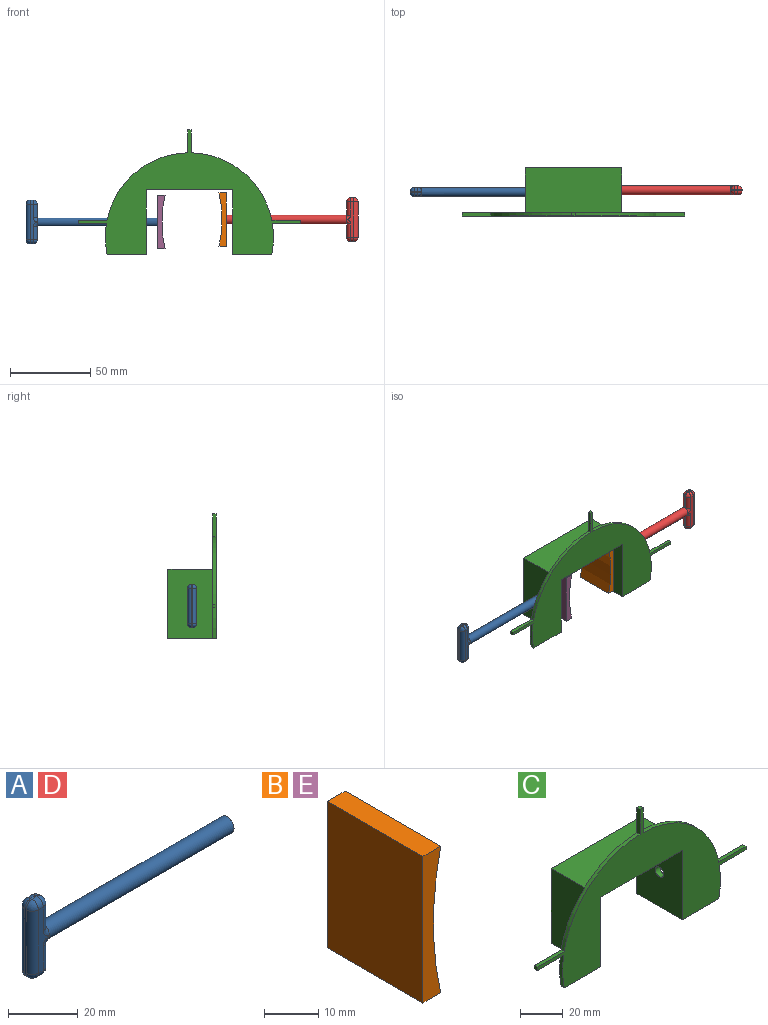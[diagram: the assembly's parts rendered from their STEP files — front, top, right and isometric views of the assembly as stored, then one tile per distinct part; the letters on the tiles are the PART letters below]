
ASSEMBLY  parts=5 mates=4
PART A: 33 faces, bbox 82x5.6x27.3 mm
  f0: plane 8.41x0.6mm, normal (1,0,0), area 5mm2, adj f1,f20,f28,f29
  f1: cylinder r=2.75mm len=75mm, axis (1,0,0), area 1295.9mm2, adj f0,f2,f8,f14,f25
  f2: plane 5.5x5.5mm, normal (1,0,0), area 23.8mm2, adj f1
  f3: plane 22.28x4.01mm, normal (0,1,0), area 47.7mm2, adj f16,f21,f25,f26,f29,f32
  f4: plane 2x0.6mm, normal (0,0,-1), area 1.2mm2, adj f19,f27,f28,f32
  f5: plane 22.28x4.01mm, normal (0,-1,0), area 48.1mm2, adj f10,f11,f14,f18,f19,f20
  f6: plane 2x0.6mm, normal (0,0,1), area 1.2mm2, adj f10,f12,f16,f17
  f7: plane 22.28x0.6mm, normal (-1,0,0), area 13.3mm2, adj f17,f18,f26,f27
  f8: plane 8.41x0.6mm, normal (1,0,0), area 5mm2, adj f1,f11,f12,f21
  f9: sphere r=2.5mm, area 9.8mm2, adj f10,f11,f12
  f10: cylinder r=2.5mm len=2.5mm, axis (1,0,0), area 7.9mm2, adj f5,f6,f9,f13
  f11: cylinder r=2.5mm len=8.41mm, axis (0,0,1), area 33mm2, adj f5,f8,f9,f14
  f12: cylinder r=2.5mm len=2.5mm, axis (0,1,0), area 2.3mm2, adj f6,f8,f9,f15
  f13: sphere r=2.5mm, area 9.8mm2, adj f10,f17,f18
  f14: bspline ~6.17x2.55mm, area 11.9mm2, adj f1,f5,f11,f20
  f15: sphere r=2.5mm, area 9.8mm2, adj f12,f16,f21
  f16: cylinder r=2.5mm len=2.5mm, axis (-1,0,0), area 7.9mm2, adj f3,f6,f15,f22
  f17: cylinder r=2.5mm len=2.5mm, axis (0,-1,0), area 2.3mm2, adj f6,f7,f13,f22
  f18: cylinder r=2.5mm len=22.28mm, axis (0,0,-1), area 87.5mm2, adj f5,f7,f13,f23
  f19: cylinder r=2.5mm len=2.5mm, axis (-1,0,0), area 7.9mm2, adj f4,f5,f23,f24
  f20: cylinder r=2.5mm len=8.41mm, axis (0,0,1), area 33mm2, adj f0,f5,f14,f24
  f21: cylinder r=2.5mm len=8.41mm, axis (0,0,-1), area 33mm2, adj f3,f8,f15,f25
  f22: sphere r=2.5mm, area 9.8mm2, adj f16,f17,f26
  f23: sphere r=2.5mm, area 9.8mm2, adj f18,f19,f27
  f24: sphere r=2.5mm, area 9.8mm2, adj f19,f20,f28
  f25: bspline ~6.17x2.55mm, area 11.9mm2, adj f1,f3,f21,f29
  f26: cylinder r=2.5mm len=22.28mm, axis (0,0,1), area 87.5mm2, adj f3,f7,f22,f30
  f27: cylinder r=2.5mm len=2.5mm, axis (0,1,0), area 2.3mm2, adj f4,f7,f23,f30
  f28: cylinder r=2.5mm len=2.5mm, axis (0,-1,0), area 2.3mm2, adj f0,f4,f24,f31
  f29: cylinder r=2.5mm len=8.41mm, axis (0,0,-1), area 33mm2, adj f0,f3,f25,f31
  f30: sphere r=2.5mm, area 9.8mm2, adj f26,f27,f32
  f31: sphere r=2.5mm, area 9.8mm2, adj f28,f29,f32
  f32: cylinder r=2.5mm len=2.5mm, axis (1,0,0), area 7.9mm2, adj f3,f4,f30,f31
PART B: 6 faces, bbox 4.7x25x33.2 mm
  f0: plane 33.19x25mm, normal (-1,0,0), area 829.9mm2, adj f1,f3,f4,f5
  f1: plane 25x4.66mm, normal (0,0,-1), area 116.5mm2, adj f0,f2,f4,f5
  f2: cylinder r=72.92mm len=33.19mm, axis (0,1,0), area 837.2mm2, adj f1,f3,f4,f5
  f3: plane 25x4.66mm, normal (0,0,1), area 116.5mm2, adj f0,f2,f4,f5
  f4: plane 33.19x4.66mm, normal (0,-1,0), area 112.2mm2, adj f0,f1,f2,f3
  f5: plane 33.19x4.66mm, normal (0,1,0), area 112.2mm2, adj f0,f1,f2,f3
PART C: 26 faces, bbox 138.8x30x77.4 mm
  f0: plane 43x28mm, normal (1,0,0), area 1180.2mm2, adj f5,f6,f8,f23,f25
  f1: plane 30x24.31mm, normal (0,0,-1), area 132.6mm2, adj f2,f7,f8,f9,f22,f23
  f2: plane 40x30mm, normal (1,0,0), area 1176.2mm2, adj f1,f3,f8,f9,f24
  f3: plane 54x30mm, normal (0,0,-1), area 1620mm2, adj f2,f4,f8,f9
  f4: plane 40x30mm, normal (-1,0,0), area 1176.2mm2, adj f3,f5,f8,f9,f25
  f5: plane 30x24.31mm, normal (0,0,-1), area 132.6mm2, adj f0,f4,f8,f9,f10,f23
  f6: plane 60x28mm, normal (0,0,1), area 1680mm2, adj f0,f7,f8,f23
  f7: plane 43x28mm, normal (-1,0,0), area 1180.2mm2, adj f1,f6,f8,f23,f24
  f8: plane 60x43mm, normal (0,1,0), area 420mm2, adj f0,f1,f2,f3,f4,f5,f6,f7
  f9: plane 138.83x77.44mm, normal (0,-1,0), area 3374.4mm2, adj f1,f2,f3,f4,f5,f10,f11,f12
  f10: cylinder r=52.42mm len=19mm, axis (0,-1,0), area 38.2mm2, adj f5,f9,f11,f23
  f11: plane 17.65x2mm, normal (0,0,-1), area 35.3mm2, adj f9,f10,f12,f23
  f12: plane 2x2mm, normal (1,0,0), area 4mm2, adj f9,f11,f13,f23
  f13: plane 18x2mm, normal (0,0,1), area 36mm2, adj f9,f12,f14,f23
  f14: cylinder r=52.42mm len=50.41mm, axis (0,-1,0), area 142mm2, adj f9,f13,f15,f23
  f15: plane 14.29x2mm, normal (1,0,0), area 28.6mm2, adj f9,f14,f16,f23
  f16: plane 2x2mm, normal (0,0,1), area 4mm2, adj f9,f15,f17,f23
  f17: plane 14.29x2mm, normal (-1,0,0), area 28.6mm2, adj f9,f16,f18,f23
  f18: cylinder r=52.42mm len=50.41mm, axis (0,-1,0), area 142mm2, adj f9,f17,f19,f23
  f19: plane 18x2mm, normal (0,0,1), area 36mm2, adj f9,f18,f20,f23
  f20: plane 2x2mm, normal (-1,0,0), area 4mm2, adj f9,f19,f21,f23
  f21: plane 17.65x2mm, normal (0,0,-1), area 35.3mm2, adj f9,f20,f22,f23
  f22: cylinder r=52.42mm len=19mm, axis (0,-1,0), area 38.2mm2, adj f1,f9,f21,f23
  f23: plane 138.83x77.44mm, normal (0,1,0), area 2954.4mm2, adj f0,f1,f5,f6,f7,f10,f11,f12
  f24: cylinder r=2.75mm len=5.5mm, axis (1,0,0), area 51.8mm2, adj f2,f7
  f25: cylinder r=2.75mm len=5.5mm, axis (-1,0,0), area 51.8mm2, adj f0,f4
PART D: same geometry as A
PART E: same geometry as B
PLACE A t=(-1.22,27.5,62.83)mm
PLACE B rot(axis=(0,1,0),180deg) t=(-304.68,28.52,-93.55)mm
PLACE C at identity fixed
PLACE D rot(axis=(0,1,0),180deg) t=(-304.68,28.52,-93.55)mm
PLACE E t=(-1.22,27.5,62.83)mm
MATE slider D.f1 <-> C.f0  axis (-1,0,0) through (-93.98,16.02,-14.6)mm
MATE slider A.f1 <-> C.f24  axis (1,0,0) through (-211.92,15,-16.13)mm
MATE fastened E.f0 <-> A.f1  axis (-1,0,0) through (-174.42,15,-16.13)mm
MATE fastened B.f0 <-> D.f1  axis (1,0,0) through (-131.48,16.02,-14.6)mm
